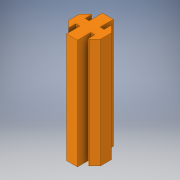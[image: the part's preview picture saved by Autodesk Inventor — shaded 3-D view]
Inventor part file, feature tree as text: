
AUTODESK INVENTOR PART (.ipt)
format: ipt  version: 2019 (Build 230136000, 136)  size: 141,824 bytes
history: native  units: in
note: dims shown in document units (in); Inventor stores cm internally (conversion verified against a paired STEP export)
features: extrude x1, fillet x1, sketch x1
ambient origin geometry x8: Origin, YZ Plane, XZ Plane, XY Plane, X Axis, Y Axis, Z Axis, Center Point
bodies: Body1 (feature_tree)
feature tree (3):
  extrude  "Extrusion2"  Depth=0.655in
  fillet  "Fillet1"  Radius=0.073in
  sketch  "Sketch1"  dims[d0=0.2in d1=0.655in d2=0.073in d4=0.1677in d9=0.121in d12=0.0in d15=0.442in d16=0.442in d20=135.0deg d21=135.0deg d24=0.2437in d25=0.655in d26=0.1372in d33=0.1372in d34=0.121in d35=0.073in d36=0.2437in d37=0.2in d38=0.2in d39=135.0deg d40=135.0deg d41=2.0in d42=0.0in d43=0.01in]
